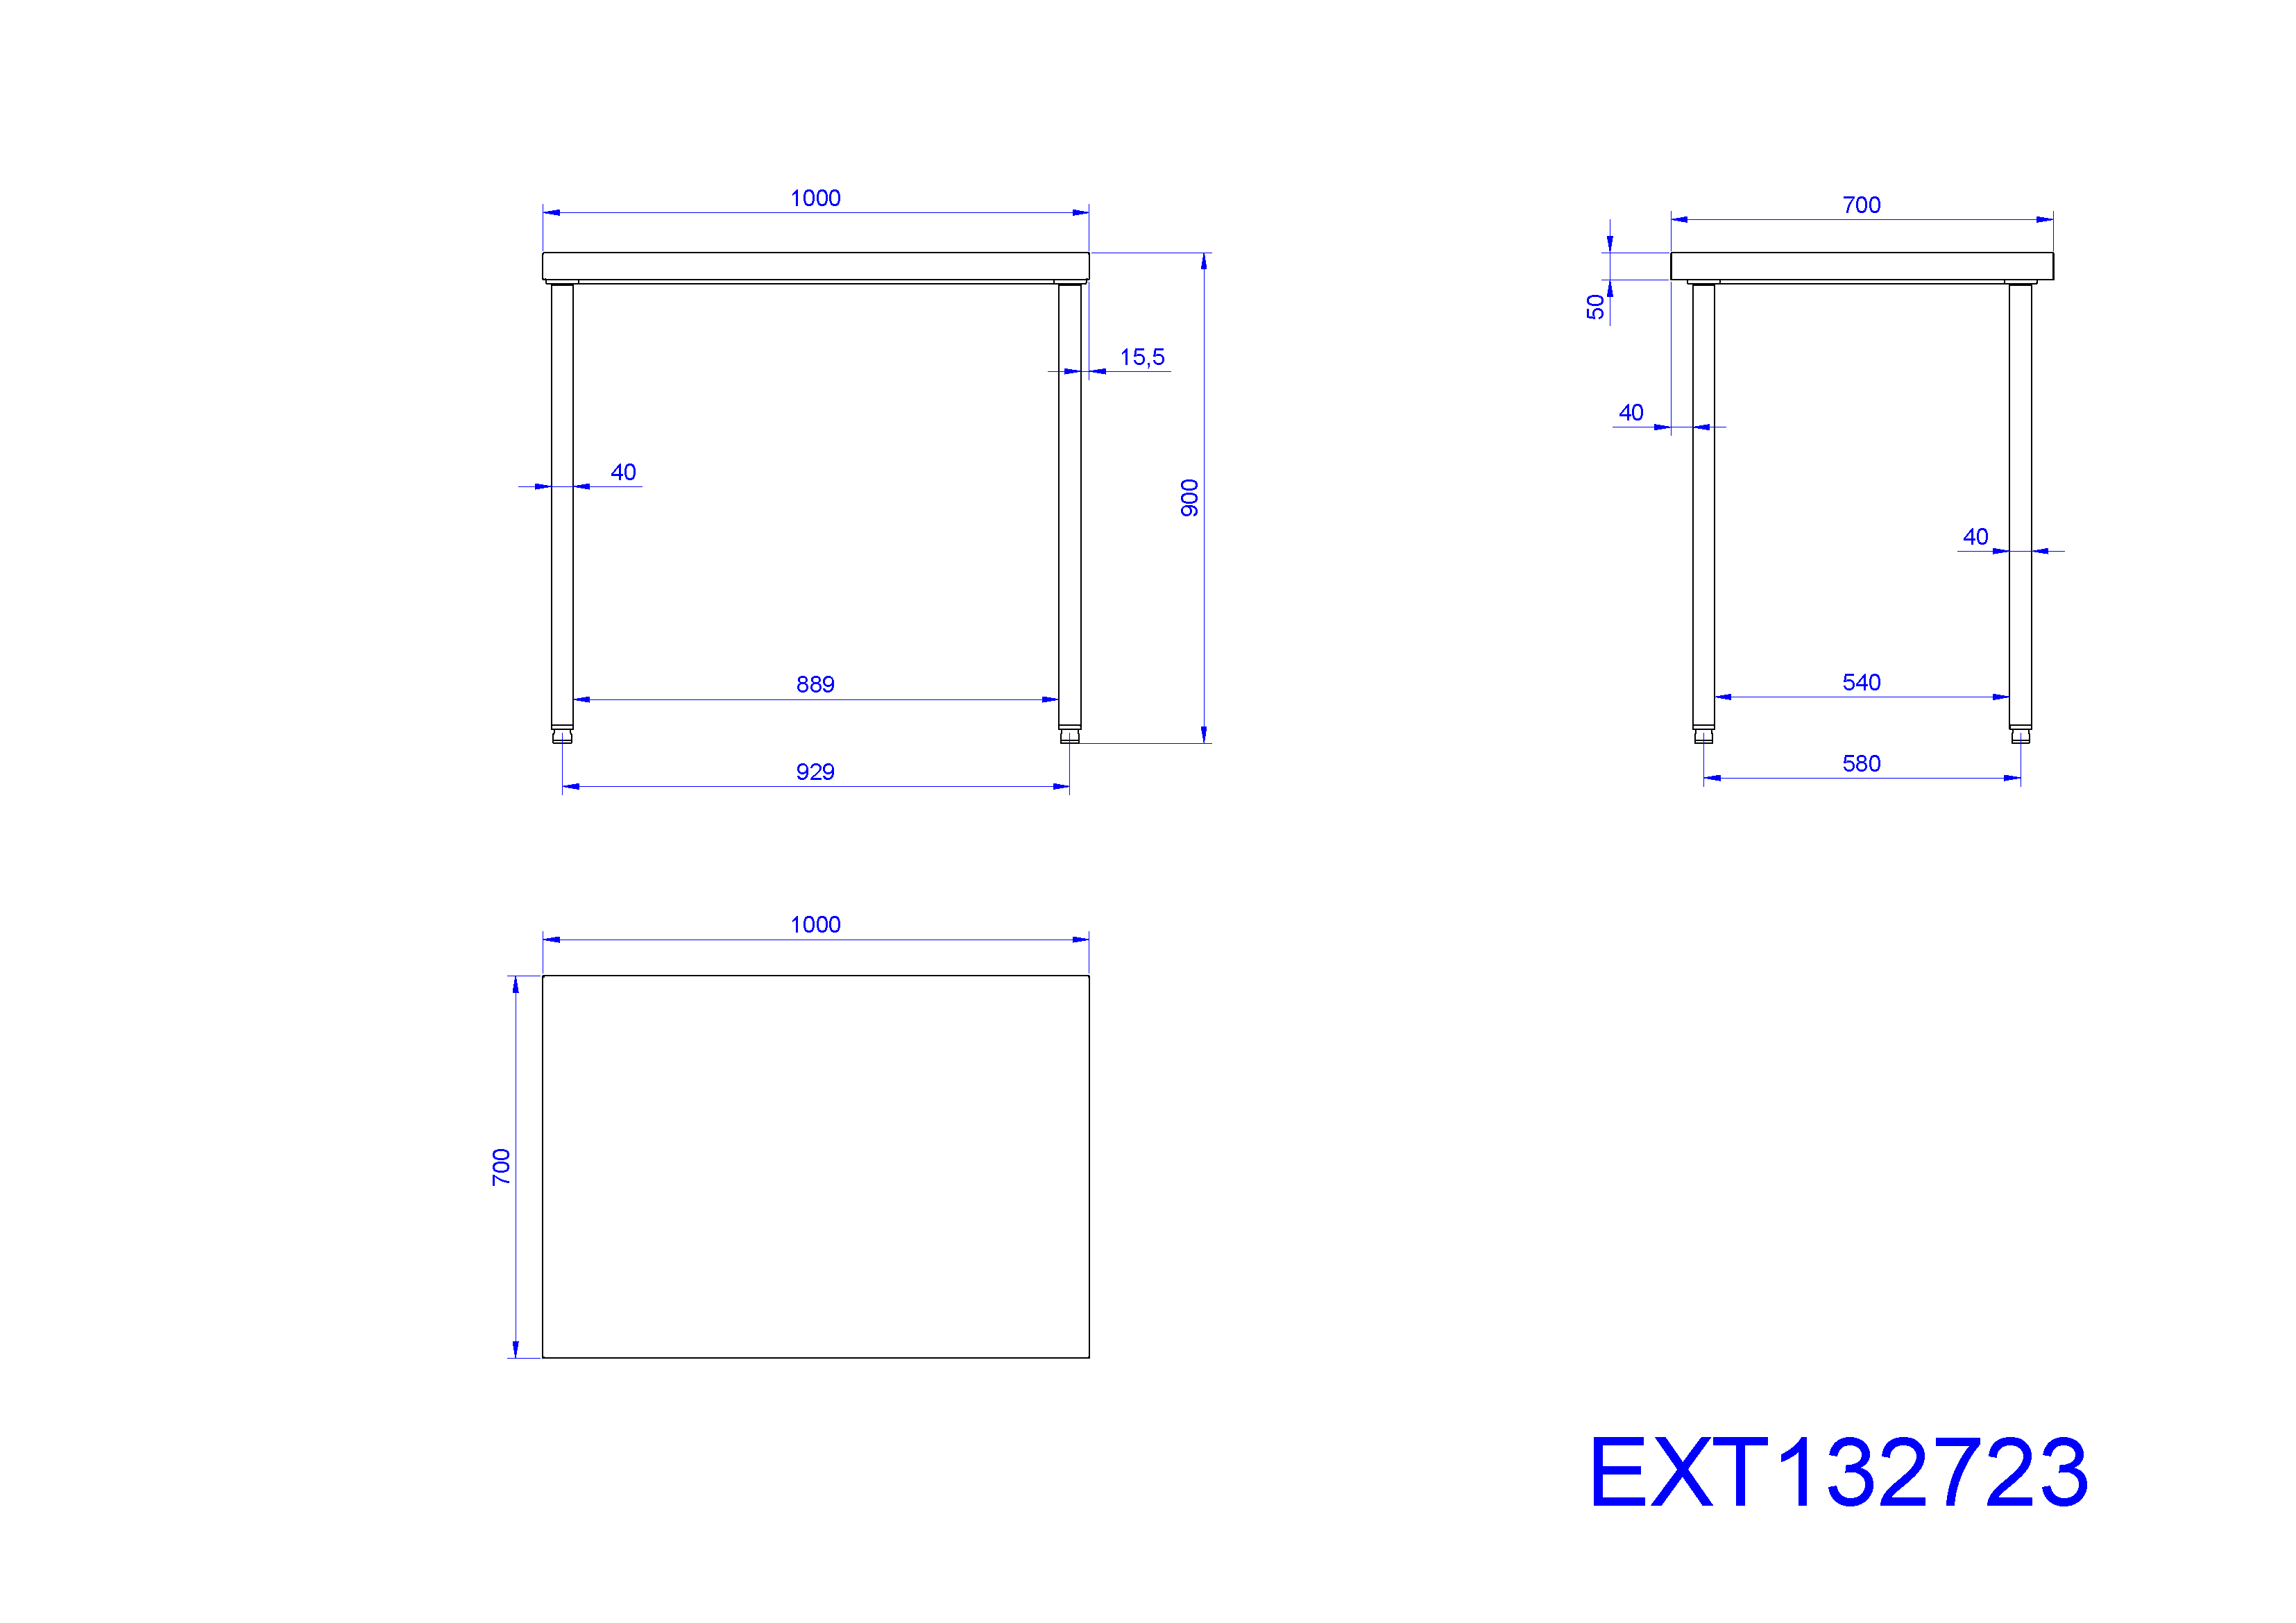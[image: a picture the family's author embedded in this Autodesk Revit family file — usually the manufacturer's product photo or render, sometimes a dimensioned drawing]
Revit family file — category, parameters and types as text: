
# Revit family: QF_ZANUSSI_133048_TG1000EN
name_source: partatom
category: Attrezzature speciali
units: mm (PartAtom-declared; Revit-internal decimal feet)

## family parameters
Basato su piano di lavoro = No
Condiviso = No
Punto di calcolo locali = No
Quota connettore circolare = Usa diametro
Sempre verticale = Sì
Taglio con vuoti quando caricato = No
Tipo di parte = Normale

## types (1)
- Standard
    Accessory = Sì
    Cold Water Size = 0 mm
    Compressed Air Pressure = 0.0 Pa
    Compressed Air Size = 0 mm
    Compressed Air Volume = 0.0 L/s
    Condensate Return Size = 0 mm
    Cycle = 0 Hz
    Depth Actual = 700 mm  [stored 2.29659 ft]
    Descrizione = WORK TABLE 1000 MM
    Direct Waste Size = 0 mm
    Gas Input Pressure = 0
    Gas KW = 0
    Gas Size = 0 mm
    HP = 0 HP
    Height Actual = 900 mm  [stored 2.95276 ft]
    Hot Water Size = 0 mm
    Item Number = 133048
    Length Actual = 1000 mm  [stored 3.28084 ft]
    Modello = TG1000EN
    Phase = 0
    Produttore = Zanussi
    Prospetto di default = 0 mm  [stored 0 ft]
    Refrigerant Compressor Remote = Sì
    Refrigeration Liquid Line Size = 0 mm  [stored 0 ft]
    Refrigeration Suction Line Size = 0 mm  [stored 0 ft]
    Steam Consumption per Hour = 0
    Steam Supply Maximum Pressure = 0.0 Pa
    Steam Supply Minimum Pressure = 0.0 Pa
    Steam Supply Size = 0 mm
    URL = http://www.zanussiprofessional.com
    URL Manufacturer = http://www.zanussiprofessional.com
    Volts = 0 V
    Watts = 0 W
    Weight = 35.00 kg

note: source unit labels omitted for Gas Input Pressure — the stored unit's dimension contradicts the parameter name (converter mislabeling)

note: [stored X ft] marks values corroborated as IEEE doubles in the binary element streams (Revit-internal decimal feet)

## geometry (parser evidence)
native form markers: Sweep x2
no freeform markers — native parametric forms only
